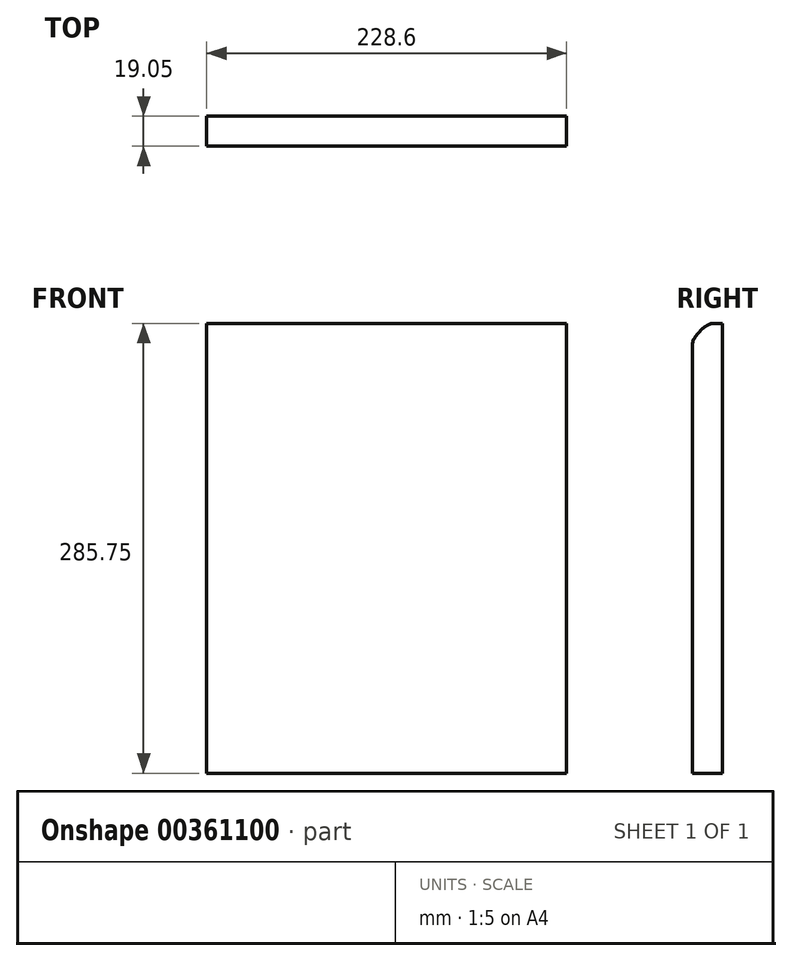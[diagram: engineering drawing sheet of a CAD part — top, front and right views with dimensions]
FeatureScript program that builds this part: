
annotation { "Feature Type Name" : "Feature", "Feature Type Description" : "" }
export const myFeature = defineFeature(function(context is Context, id is Id, definition is map)
    precondition{}
    {
        {
            var Q0;
            Q0=qCreatedBy(makeId("Front.planeOp"),FACE);
            var sketch = newSketch(context, id + "F0", { "sketchPlane" : qUnion([Q0])});
            skLineSegment(sketch, "E0.bottom", {"start": v(0, 0) * mm, "end": v(-228.6, 0) * mm});
            skLineSegment(sketch, "E0.top", {"start": v(0, 285.75) * mm, "end": v(-228.6, 285.75) * mm});
            skLineSegment(sketch, "E0.left", {"start": v(0, 0) * mm, "end": v(0, 228.6) * mm});
            skLineSegment(sketch, "E0.right", {"start": v(-228.6, 0) * mm, "end": v(-228.6, 228.6) * mm});
            skLineSegment(sketch, "E1.top", {"start": v(-228.6, 0) * mm, "end": v(0, 0) * mm});
            skLineSegment(sketch, "E1.left", {"start": v(-228.6, 228.6) * mm, "end": v(-228.6, 0) * mm});
            skLineSegment(sketch, "E1.right", {"start": v(0, 285.75) * mm, "end": v(0, 0) * mm});
            skPoint(sketch, "E2.end.orphan", {"position": v(-114.3, 285.75) * mm});
            skPoint(sketch, "E2.start.orphan", {"position": v(-114.3, 228.6) * mm});
            skPoint(sketch, "E3.bottom.end.orphan", {"position": v(-215.9, 285.75) * mm});
            skPoint(sketch, "E4.orphan", {"position": v(-215.9, 228.6) * mm});
            skLineSegment(sketch, "E5", {"start": v(-228.6, 0) * mm, "end": v(-228.6, 285.75) * mm});
            skSolve(sketch);
        }
        {
            var Q0;
            Q0=makeQuery(id+"F0.imprint","IMPRINT",FACE,{"disambiguationData":[TD([[makeQuery(id+"F0.imprint","IMPRINT",EDGE,{"derivedFrom":sQuery(id+"F0.wireOp",EDGE,"E1.top")}),1.0]])]});
            var Q1;
            Q1=makeQuery(id+"F0.imprint","IMPRINT",FACE,{"disambiguationData":[TD([[makeQuery(id+"F0.imprint","IMPRINT",EDGE,{"derivedFrom":sQuery(id+"F0.wireOp",EDGE,"E3.bottom")}),-1.0]])]});
            var Q2;
            Q2=makeQuery(id+"F0.imprint","IMPRINT",FACE,{"disambiguationData":[TD([[makeQuery(id+"F0.imprint","IMPRINT",EDGE,{"derivedFrom":sQuery(id+"F0.wireOp",EDGE,"fa84920b-f169-4927-aaa2-2baba05e7e05.bottom")}),1.0]])]});
            var Q3;
            Q3=makeQuery(id+"F0.imprint","IMPRINT",FACE,{"disambiguationData":[TD([[makeQuery(id+"F0.imprint","IMPRINT",EDGE,{"derivedFrom":sQuery(id+"F0.wireOp",EDGE,"E0.top")}),1.0]])]});
            extrude(context, id + "F1", {"entities" : qUnion([Q0, Q1, Q2, Q3]), "depth" : 19.05 * mm});
        }
        {
            var Q0;
            Q0=makeQuery(id+"F1.opExtrude","CAP_EDGE",EDGE,{"disambiguationData":[OSD([sQuery(id+"F0.wireOp",EDGE,"E0.top"),sQuery(id+"F0.wireOp",EDGE,"fa84920b-f169-4927-aaa2-2baba05e7e05.bottom"),sQuery(id+"F0.wireOp",EDGE,"E3.bottom")])],"isStart":false});
            fillet(context, id + "F2", {"entities" : qUnion([Q0]), "radius" : 12.7 * mm, "tangentPropagation" : true, "rho" : 0.25, "crossSection" : FilletCrossSection.CONIC, "allowEdgeOverflow" : false});
        }
    });
